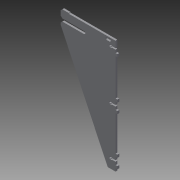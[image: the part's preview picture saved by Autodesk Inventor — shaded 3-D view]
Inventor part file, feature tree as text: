
AUTODESK INVENTOR PART (.ipt)
format: ipt  version: 2015 (Build 190159000, 159)  size: 187,904 bytes
history: native  units: mm
features: extrude x1, sketch x1
ambient origin geometry x8: Origin, YZ Plane, XZ Plane, XY Plane, X Axis, Y Axis, Z Axis, Center Point
bodies: Solid1 (feature_tree)
feature tree (2):
  extrude  "Extrusion1"  [1 undecoded]
  sketch  "Sketch1"  dims[d0=6.0mm d1=0.0mm]
note: 1 required parameter value undecoded (feature->parameter linkage not recoverable at this tier; creation-order binding heuristic only, values carry confidence <= 0.55)
